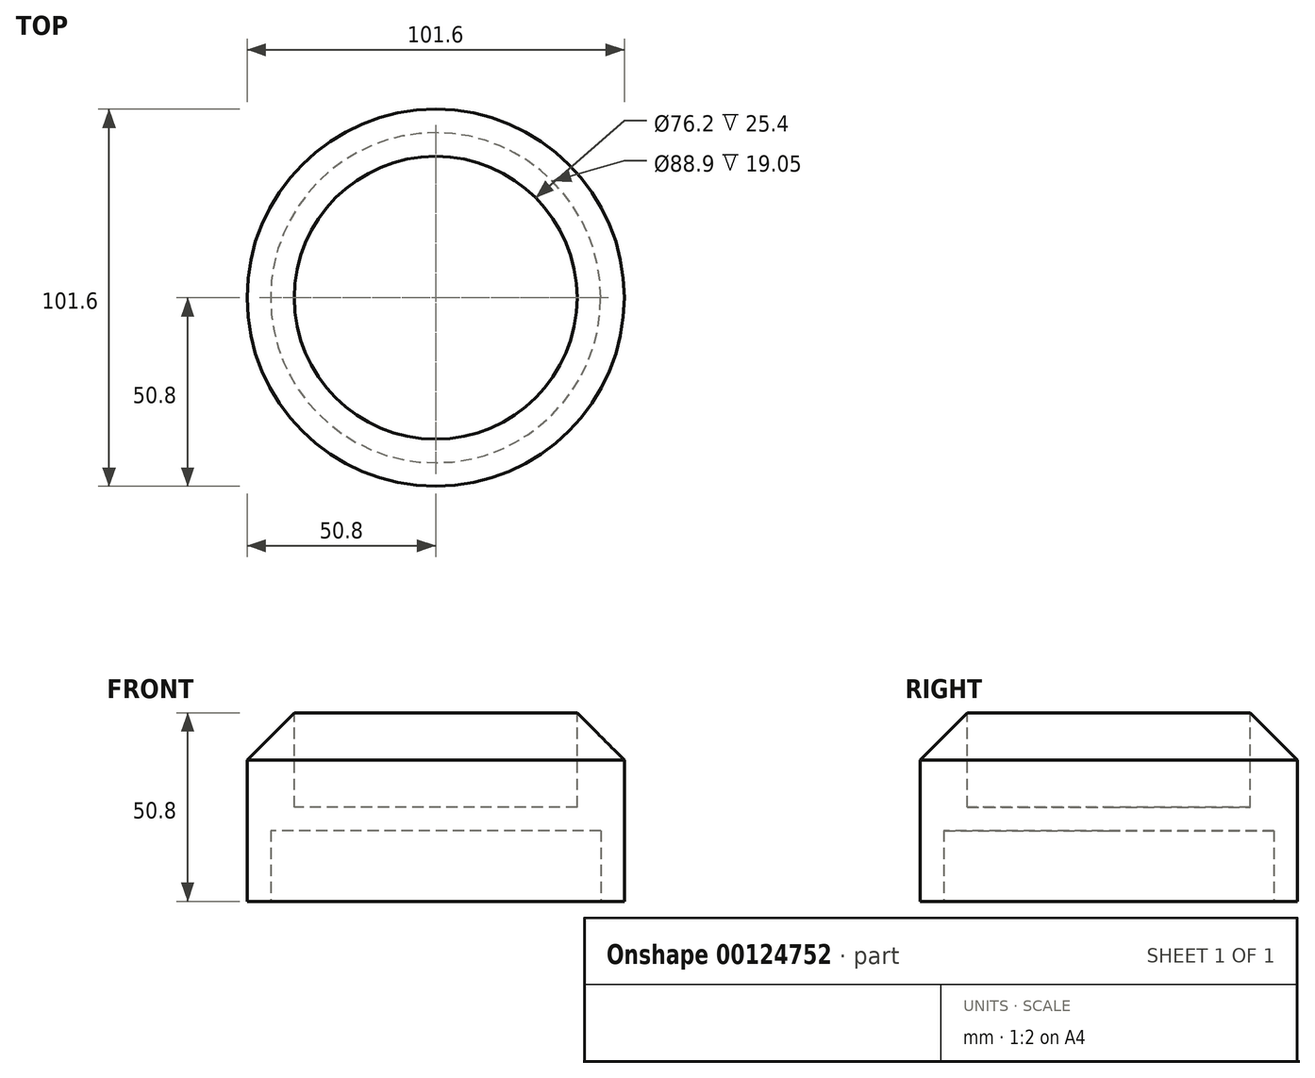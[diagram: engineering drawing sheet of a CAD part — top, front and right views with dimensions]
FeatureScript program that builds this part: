
annotation { "Feature Type Name" : "Feature", "Feature Type Description" : "" }
export const myFeature = defineFeature(function(context is Context, id is Id, definition is map)
    precondition{}
    {
        {
            var Q0;
            Q0=qCreatedBy(makeId("Top.planeOp"),FACE);
            var sketch = newSketch(context, id + "F0", { "sketchPlane" : qUnion([Q0])});
            skCircle(sketch, "E0", {"center": v(0, 0) * mm, "radius": 50.8 * mm});
            skSolve(sketch);
        }
        {
            var Q0;
            Q0 = qSketchRegion(id + "F0", true);
            extrude(context, id + "F1", {"entities" : qUnion([Q0]), "depth" : 50.8 * mm});
        }
        {
            var Q0;
            Q0=makeQuery(id+"F1.opExtrude","CAP_EDGE",EDGE,{"disambiguationData":[OSD([sQuery(id+"F0.wireOp",EDGE,"E0")])],"isStart":false});
            chamfer(context, id + "F2", {"entities" : qUnion([Q0]), "width" : 12.7 * mm, "tangentPropagation" : true});
        }
        {
            var Q0;
            Q0=makeQuery(id+"F1.opExtrude","CAP_FACE",FACE,{"disambiguationData":[OSD([sQuery(id+"F0.wireOp",EDGE,"E0")])],"isStart":false});
            extrude(context, id + "F3", {"entities" : qUnion([Q0]), "operationType" : NewBodyOperationType.REMOVE, "oppositeDirection" : true, "depth" : 25.4 * mm});
        }
        {
            var Q0;
            Q0=makeQuery(id+"F1.opExtrude","CAP_FACE",FACE,{"disambiguationData":[OSD([sQuery(id+"F0.wireOp",EDGE,"E0")])],"isStart":true});
            shell(context, id + "F4", {"entities" : qUnion([Q0]), "thickness" : 6.35 * mm});
        }
    });
